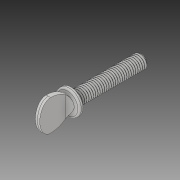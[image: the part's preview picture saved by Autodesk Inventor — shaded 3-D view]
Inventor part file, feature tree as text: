
AUTODESK INVENTOR PART (.ipt)
format: ipt  version: 2018 (Build 220112000, 112)  size: 979,456 bytes
history: native  units: in
note: dims shown in document units (in); Inventor stores cm internally (conversion verified against a paired STEP export)
features: fillet x1
ambient origin geometry x8: Origin, YZ Plane, XZ Plane, XY Plane, X Axis, Y Axis, Z Axis, Center Point
bodies: Solid1 (feature_tree)
feature tree (1):
  fillet  "Fillet14"  [1 undecoded]
note: 1 required parameter value undecoded (feature->parameter linkage not recoverable at this tier; creation-order binding heuristic only, values carry confidence <= 0.55)
